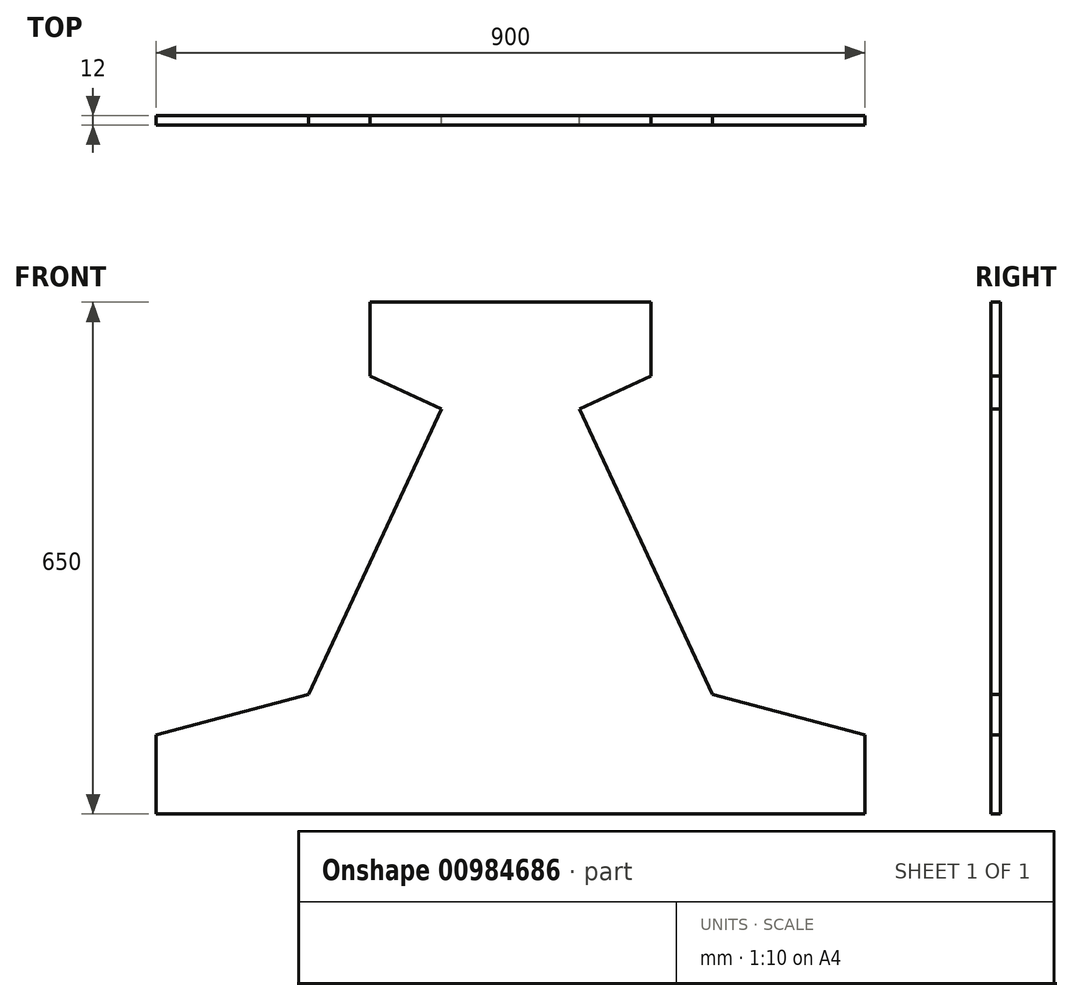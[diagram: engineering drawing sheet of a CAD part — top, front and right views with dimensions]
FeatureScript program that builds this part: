
annotation { "Feature Type Name" : "Feature", "Feature Type Description" : "" }
export const myFeature = defineFeature(function(context is Context, id is Id, definition is map)
    precondition{}
    {
        {
            var Q0;
            Q0=qCreatedBy(makeId("Front.planeOp"),FACE);
            var sketch = newSketch(context, id + "F0", { "sketchPlane" : qUnion([Q0])});
            skLineSegment(sketch, "E0.top", {"start": v(-247.84, -234.92) * mm, "end": v(652.16, -234.92) * mm});
            skLineSegment(sketch, "E0.left", {"start": v(-247.84, -134.92) * mm, "end": v(-247.84, -234.92) * mm});
            skLineSegment(sketch, "E0.right", {"start": v(652.16, -134.92) * mm, "end": v(652.16, -234.92) * mm});
            skLineSegment(sketch, "E1", {"start": v(-247.84, -134.92) * mm, "end": v(-54.65, -83.16) * mm});
            skLineSegment(sketch, "E2", {"start": v(458.98, -83.16) * mm, "end": v(652.16, -134.92) * mm});
            skLineSegment(sketch, "E3", {"start": v(-54.65, -83.16) * mm, "end": v(114.4, 279.37) * mm});
            skLineSegment(sketch, "E4", {"start": v(114.4, 279.37) * mm, "end": v(23.76, 321.63) * mm});
            skLineSegment(sketch, "E5", {"start": v(23.76, 321.63) * mm, "end": v(23.76, 415.08) * mm});
            skLineSegment(sketch, "E6", {"start": v(23.76, 415.08) * mm, "end": v(380.56, 415.08) * mm});
            skLineSegment(sketch, "E7", {"start": v(380.56, 415.08) * mm, "end": v(380.56, 321.63) * mm});
            skLineSegment(sketch, "E8", {"start": v(380.56, 321.63) * mm, "end": v(289.93, 279.37) * mm});
            skLineSegment(sketch, "E9", {"start": v(289.93, 279.37) * mm, "end": v(458.98, -83.16) * mm});
            skSolve(sketch);
        }
        {
            var Q0;
            Q0=qSketchRegion(id+"F0",true);
            extrude(context, id + "F1", {"entities" : qUnion([Q0]), "depth" : 12 * mm, "offsetDistance" : 25.4 * mm});
        }
    });
